# Revit family: BE_99620_de_DE
name_source: partatom
category: Leuchten
revit_build: Autodesk Revit 2015 (Build: 20150704_0715(x64)
units: mm (PartAtom-declared; Revit-internal decimal feet)

## types (2) — shared parameters
Aktualisierung = 2015-12-09T04:08:32
BEGA_Dummy = Nein
BEGA_IES = Ja
BEGA_Intern = Ja
BEGA_Intern_Konstruktion = Ja
BEGA_Intern_an = Ja
BEGA_Intern_aus = Ja
Beschreibung = Pollerleuchtenrohr
Beschreibung_Sonderanfertigung = Hier können Sie Informationen zur Sonderanfertigung eintragen.
CE_Konformität = ja
Einbauöffnung = 140 mm
Gewicht = 3.5 kg
Hersteller = BEGA
Lastklassifizierung = Beleuchtung
Logo = BEGA_Logo.png
Material_02 = BEGA_Oberfläche_Silber_matt
Produktdatenblatt = http://www.bega.de
Scheinlast = 0 VA
Sonderanfertigung = Nein
Typenbild = 99620.png
URL = http://www.bega.de
zero-valued in all types: Vorgabe-Ansicht

## per-type parameters (varying)
| type | Bestellnummer | M_A | M_G | Modell |
| BEGA_99620_Grafit | 99620 | Nein | Ja | 99620 |
| BEGA_99620_Silber | 99620A | Ja | Nein | 99620A |
